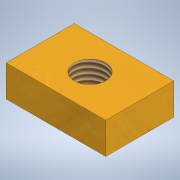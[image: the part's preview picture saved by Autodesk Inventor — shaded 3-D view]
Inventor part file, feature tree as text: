
AUTODESK INVENTOR PART (.ipt)
format: ipt  version: 2020 (Build 240168000, 168)  size: 104,960 bytes
history: native  units: mm
features: extrude x1, thread x1, sketch x1
ambient origin geometry x8: Origin, YZ Plane, XZ Plane, XY Plane, X Axis, Y Axis, Z Axis, Center Point
bodies: Solid1 (feature_tree)
feature tree (3):
  extrude  "Extrusion1"  Depth=6.5mm
  thread  "Thread1"  [1 undecoded]
  sketch  "Sketch1"  dims[d0=9.5mm d1=6.5mm d2=3.0mm d3=3.0mm d4=0.0mm d5=3.0mm d6=0.0mm]
note: 1 required parameter value undecoded (feature->parameter linkage not recoverable at this tier; creation-order binding heuristic only, values carry confidence <= 0.55)
